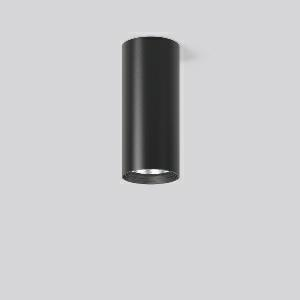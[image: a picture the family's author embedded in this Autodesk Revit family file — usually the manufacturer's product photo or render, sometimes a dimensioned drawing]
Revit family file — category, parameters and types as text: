
# Revit family: heledon_mini_a_931209_003_1_07f0
name_source: partatom
category: Lighting Fixtures
units: mm (PartAtom-declared; Revit-internal decimal feet)

## family parameters
Cut with Voids When Loaded = No
Host = Face
Light Source = No
Part Type = Normal
Room Calculation Point = No
Round Connector Dimension = Use Diameter
Shared = No

## types (1)
- HELEDON mini A (1 x LED Modul 940, 3700 lm, 4000)
    Apparent Load = 29 VA
    Approval mark = CE
    CIE Flux Codes = 99 100 100 100 100
    Color Rendering = 92
    Color Temperature = 4000
    Default Elevation = 1800 mm
    Description = Series: HELEDON mini
Cylindrical surface-mounted downlight. Housing: die-cast aluminium, powder-coated. Internal ceiling frame polycarbonate with bayonet mounting. Black plastic ring and recessed LED to prevent glare from the side. Optical assembly with reflector made of MIRO-Silver with 98% total light reflection for outstanding efficiency - can be changed without tools. Best colour rendering index Ra>90. Suitable for Ceiling mounting. Easy installation with a separate ceiling frame with bayonet mounting and plug connection. Driver integrated. Connected via plug-in connector. High quality converter without flickering and stroboscopic effect. The following accessories can be mounted without use of tools: interchangeable lenses, decorative glasses, honeycomb louvre, clear and frosted diffusers, white interchangeable plastic ring. 
Colour: deep black, matt (RAL 9005)
Diameter: 87 mm
Height: 197 mm
Lamp: LED
Socket: without socket
Colour temperature: 4000K
Colour rendering index (CRI): 92
System power: 29 W
Rated luminous flux: 3700 lm
Luminous efficiency: 128 lm/W
Control gear: Regulated power supply
Protection class: I
Type of protection: IP 20
    Height = 197 mm
    Lamp = 1 x LED Modul 940
    Lamp Light Flux = 3700 lm
    Lamp count = 1
    Length = 87 mm
    Lifetime = 50000 h
    Luminous efficacy = 128 lm/W
    Manufacturer = RZB
    ModVariant = No
    Model = 931209.003.1
    Mounting Place = Ceiling
    Mounting Type = Surface mounted
    Number of Poles = 1
    OnlyDefault = Yes
    Power Factor = 1
    Product Name = HELEDON mini A
    Product group = Surface mounted downlights
    ProductGroupID = 302
    Protection Class = Protection class I
    Protection Degree = IP 20
    RLX_Detail_Level = 1
    RLX_Emergency_Light_Flux = 0 lm
    RLX_Emergency_Type = 0
    RLX_Emergency_Type_DB = No
    RlxData = <blob elided: 107237 chars, md5=c3ef65a8>
    Socket = socket
    Standby Power = 0 W
    System Light Flux = 3700 lm
    System Power = 29 W
    Type Comments = Product without accessories
    Type Image = 931188.003.jpg
    URL = http://relux.com
    VarID = ---
    Voltage = 230 V
    Voltage Range = 220-240 V
    Weight = 0.00 kg
    Width = 0 mm  [stored 0 ft]

note: [stored X ft] marks values corroborated as IEEE doubles in the binary element streams (Revit-internal decimal feet)

## geometry (parser evidence)
native form markers: Blend x4, Sweep x9
no freeform markers — native parametric forms only
